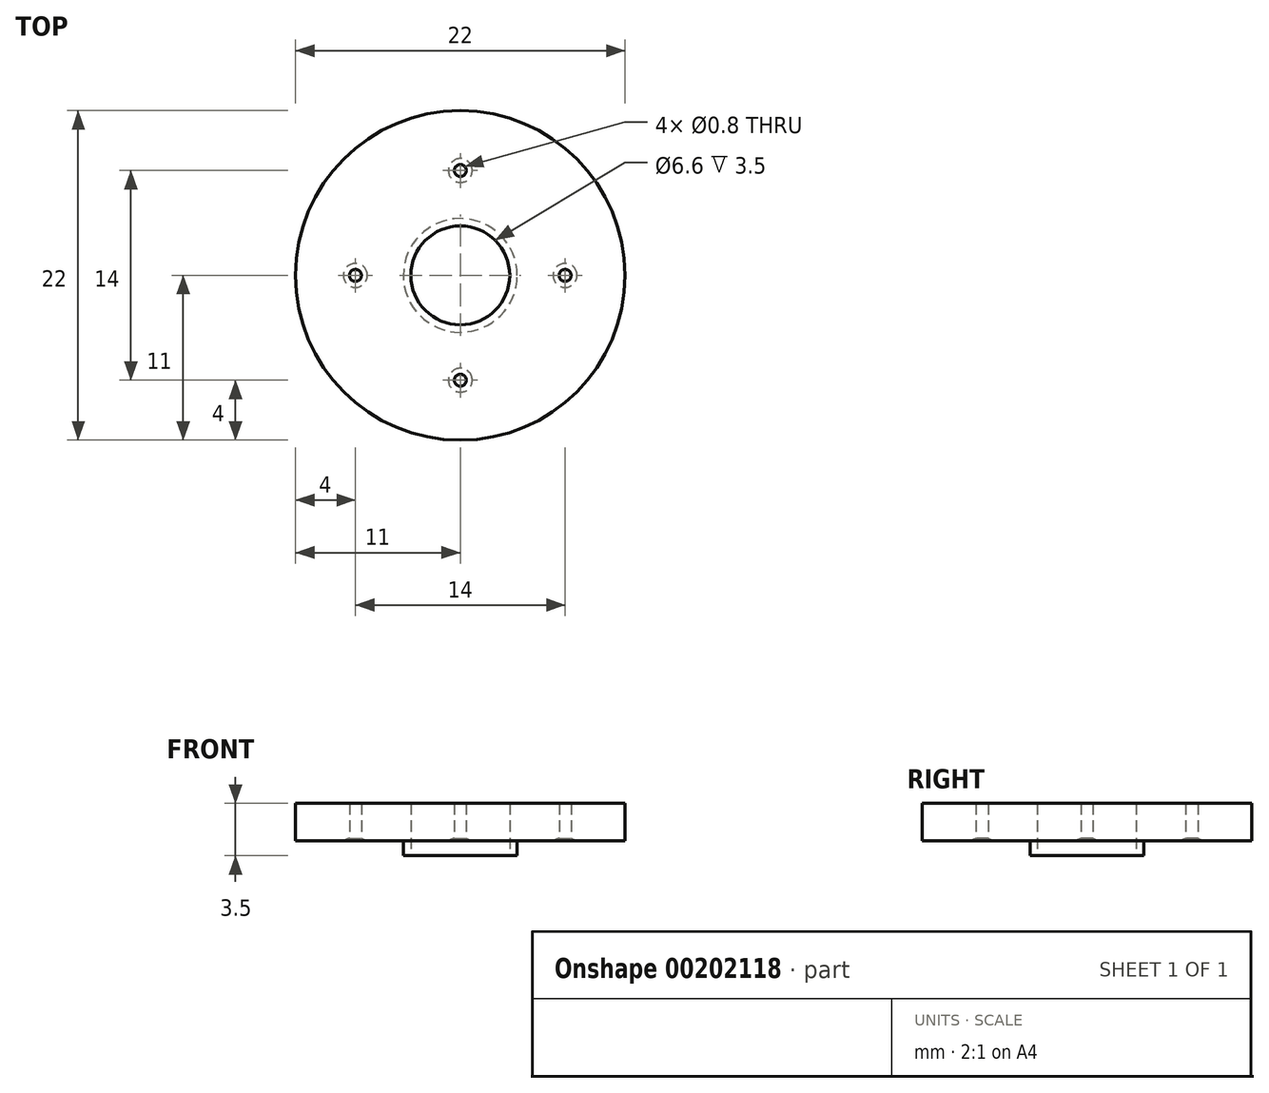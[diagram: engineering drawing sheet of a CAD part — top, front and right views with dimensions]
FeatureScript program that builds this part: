
annotation { "Feature Type Name" : "Feature", "Feature Type Description" : "" }
export const myFeature = defineFeature(function(context is Context, id is Id, definition is map)
    precondition{}
    {
        {
            var Q0;
            Q0=qCreatedBy(makeId("Top.planeOp"),FACE);
            var sketch = newSketch(context, id + "F0", { "sketchPlane" : qUnion([Q0])});
            skCircle(sketch, "E0", {"center": v(0, 0) * mm, "radius": 11 * mm});
            skPoint(sketch, "E1", {"position": v(0, 7) * mm});
            skPoint(sketch, "E2.1.0", {"position": v(7, 0) * mm});
            skPoint(sketch, "E2.2.0", {"position": v(0, -7) * mm});
            skPoint(sketch, "E2.3.0", {"position": v(-7, 0) * mm});
            skLineSegment(sketch, "E2.anchor1", {"start": v(0, 0) * mm, "end": v(0, 7) * mm, "construction": true});
            skLineSegment(sketch, "E2.anchor2", {"start": v(0, 0) * mm, "end": v(-7, 0) * mm, "construction": true});
            skCircle(sketch, "E3", {"center": v(0, 0) * mm, "radius": 3.8 * mm});
            skCircle(sketch, "E4", {"center": v(0, 0) * mm, "radius": 3.3 * mm});
            skSolve(sketch);
        }
        {
            var Q0;
            Q0 = qSketchRegion(id + "F0", true);
            var Q1;
            Q1=makeQuery(id+"F0.imprint","IMPRINT",FACE,{"disambiguationData":[TD([[makeQuery(id+"F0.imprint","IMPRINT",EDGE,{"derivedFrom":sQuery(id+"F0.wireOp",EDGE,"E3")}),1.0]])]});
            var Q2;
            Q2=makeQuery(id+"F0.imprint","IMPRINT",FACE,{"disambiguationData":[TD([[makeQuery(id+"F0.imprint","IMPRINT",EDGE,{"derivedFrom":sQuery(id+"F0.wireOp",EDGE,"E3")}),-1.0]])]});
            extrude(context, id + "F1", {"entities" : qUnion([Q0, Q1, Q2]), "depth" : 2.5 * mm});
        }
        {
            var Q0;
            Q0=makeQuery(id+"F0.imprint","IMPRINT",FACE,{"disambiguationData":[TD([[makeQuery(id+"F0.imprint","IMPRINT",EDGE,{"derivedFrom":sQuery(id+"F0.wireOp",EDGE,"E3")}),1.0]])]});
            extrude(context, id + "F2", {"entities" : qUnion([Q0]), "operationType" : NewBodyOperationType.ADD, "oppositeDirection" : true, "depth" : 1 * mm});
        }
        {
            var Q0;
            Q0=sQuery(id+"F0.wireOp",VERTEX,"E2.2.0");
            var Q1;
            Q1=sQuery(id+"F0.wireOp",VERTEX,"E2.1.0");
            var Q2;
            Q2=sQuery(id+"F0.wireOp",VERTEX,"E1");
            var Q3;
            Q3=sQuery(id+"F0.wireOp",VERTEX,"E2.3.0");
            var Q4;
            Q4=makeQuery(id+"F1.opExtrude","SWEPT_BODY",BODY,{"disambiguationData":[OSD([sQuery(id+"F0.wireOp",EDGE,"E0"),sQuery(id+"F0.wireOp",EDGE,"E4")])]});
            hole(context, id + "F3", {"style" : HoleStyle.C_SINK, "endStyle" : HoleEndStyle.THROUGH, "oppositeDirection" : true, "holeDiameter" : 0.8 * mm, "cSinkDiameter" : 1.6 * mm, "cSinkAngle" : 135 * degree, "locations" : qUnion([Q0, Q1, Q2, Q3]), "scope" : qUnion([Q4]), "isTappedThrough" : true});
        }
    });
